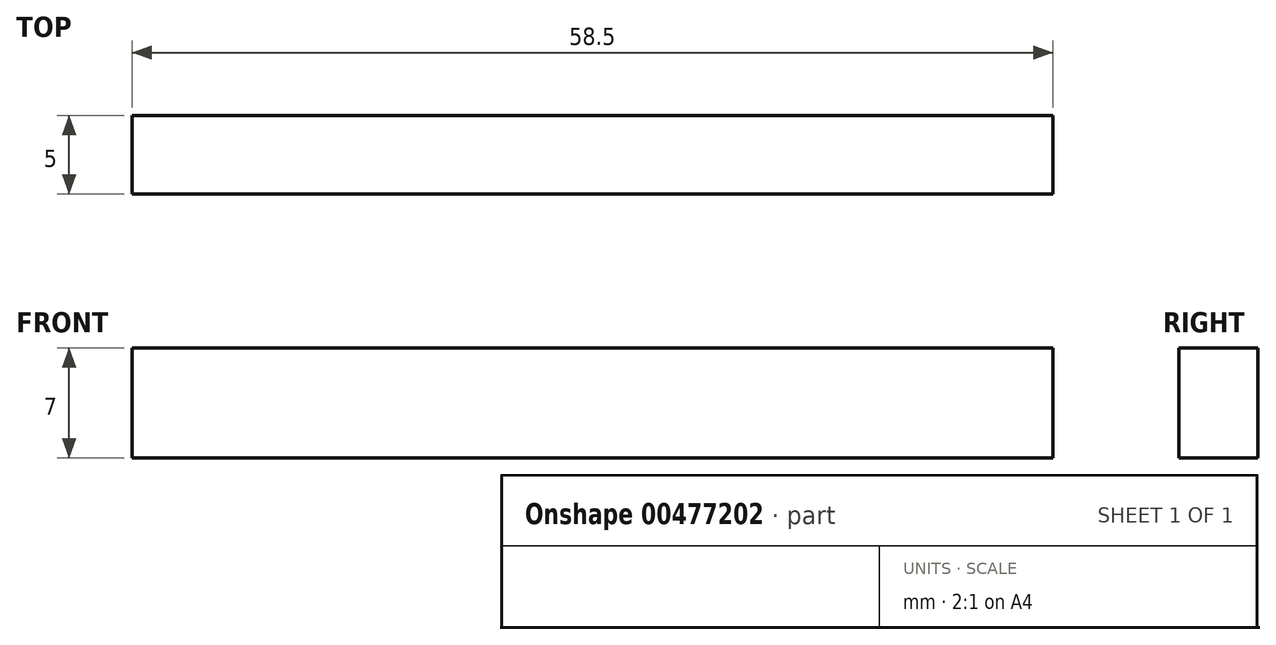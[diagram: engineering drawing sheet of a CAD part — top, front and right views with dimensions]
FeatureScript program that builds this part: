
annotation { "Feature Type Name" : "Feature", "Feature Type Description" : "" }
export const myFeature = defineFeature(function(context is Context, id is Id, definition is map)
    precondition{}
    {
        {
            var Q0;
            Q0=qCreatedBy(makeId("Right.planeOp"),FACE);
            var sketch = newSketch(context, id + "F0", { "sketchPlane" : qUnion([Q0])});
            skLineSegment(sketch, "E0.bottom", {"start": v(-25, -3) * mm, "end": v(-20, -3) * mm});
            skLineSegment(sketch, "E0.top", {"start": v(-25, -10) * mm, "end": v(-20, -10) * mm});
            skLineSegment(sketch, "E0.left", {"start": v(-25, -3) * mm, "end": v(-25, -10) * mm});
            skLineSegment(sketch, "E0.right", {"start": v(-20, -3) * mm, "end": v(-20, -10) * mm});
            skLineSegment(sketch, "E1", {"start": v(-20, -3) * mm, "end": v(-20, 0) * mm});
            skLineSegment(sketch, "E2", {"start": v(-20, 0) * mm, "end": v(0, 0) * mm});
            skLineSegment(sketch, "E3", {"start": v(0, 0) * mm, "end": v(0, 0) * mm});
            skLineSegment(sketch, "E4.top", {"start": v(-25, -6) * mm, "end": v(-35, -6) * mm});
            skLineSegment(sketch, "E4.left", {"start": v(-25, -3) * mm, "end": v(-25, -6) * mm});
            skLineSegment(sketch, "E4.right", {"start": v(-35, -5) * mm, "end": v(-35, -6) * mm});
            skLineSegment(sketch, "E5", {"start": v(-35, -5) * mm, "end": v(-25, -5) * mm});
            skSolve(sketch);
        }
        {
            var Q0;
            Q0=makeQuery(id+"F0.imprint","IMPRINT",FACE,{"disambiguationData":[TD([[makeQuery(id+"F0.imprint","IMPRINT",EDGE,{"derivedFrom":sQuery(id+"F0.wireOp",EDGE,"E0.bottom")}),-1.0]])]});
            extrude(context, id + "F1", {"entities" : qUnion([Q0]), "endBound" : BoundingType.SYMMETRIC, "depth" : 119 * mm});
        }
        {
            var Q0;
            {var subQ0=sQuery(id+"F0.wireOp",EDGE,"E4.top");Q0=makeQuery(id+"F0.imprint","IMPRINT",FACE,{"disambiguationData":[TD([[makeQuery(id+"F0.imprint","IMPRINT",EDGE,{"derivedFrom":subQ0}),-1.0]])]});}
            extrude(context, id + "F2", {"entities" : qUnion([Q0]), "endBound" : BoundingType.SYMMETRIC, "depth" : 2 * mm});
        }
        {
            var Q0;
            Q0=qCreatedBy(makeId("Right.planeOp"),FACE);
            var sketch = newSketch(context, id + "F3", { "sketchPlane" : qUnion([Q0])});
            skLineSegment(sketch, "E6.bottom", {"start": v(-37.57, 6.84) * mm, "end": v(-11.94, 6.84) * mm});
            skLineSegment(sketch, "E6.top", {"start": v(-37.57, -19.78) * mm, "end": v(-11.94, -19.78) * mm});
            skLineSegment(sketch, "E6.left", {"start": v(-37.57, 6.84) * mm, "end": v(-37.57, -19.78) * mm});
            skLineSegment(sketch, "E6.right", {"start": v(-11.94, 6.84) * mm, "end": v(-11.94, -19.78) * mm});
            skSolve(sketch);
        }
        {
            var Q0;
            Q0=qSketchRegion(id+"F3",true);
            extrude(context, id + "F4", {"entities" : qUnion([Q0]), "operationType" : NewBodyOperationType.REMOVE, "endBound" : BoundingType.SYMMETRIC, "oppositeDirection" : true, "depth" : 2 * mm});
        }
        {
            var Q0;
            Q0=qSketchRegion(id+"F3",true);
            extrude(context, id + "F5", {"entities" : qUnion([Q0]), "operationType" : NewBodyOperationType.REMOVE, "depth" : 70 * mm});
        }
    });
